# Revit family: Door-Exterior-Simpson-Nantucket-Full_Glass-Single
name_source: partatom
category: Doors
revit_build: Autodesk Revit Architecture 2012 (Build: 20110916_2132(x64)
units: mm (PartAtom-declared; Revit-internal decimal feet)

## types (219) — shared parameters
Assembly Code = B2030230
Construction Type = Wood
Frame = Wood - Simpson Doors - Douglas Fir
Frame Projection Ext. = 0' - 1"
Frame Projection Int. = 0' - 1"
Frame Type = Frame : Standard
Frame Width = 0' - 3"
Function = Exterior
Glass = Glass - Simpson Doors - Clear
Manufacturer = Simpsons Door Company
Ovolo Construction = Yes
Panel = Wood - Simpson Doors - Douglas Fir
Panel Stile Width = 0' - 5"
Product Documentation Link = http://www.simpsondoor.com
Product Page URL = http://www.simpsondoor.com
Thickness = 0' - 1 3/4"
Thickness Note = comes in 1 3/4" and 2 1/4" Thickness. Default is set to 1 3/4"
URL = http://www.simpsondoor.com
Wall Closure = By host

## per-type parameters (varying)
| type | Bottom Rail Height | Description | Height | Horizontal Outside Muntin | Middle Rail | Model | Number of Horizontal Muntins | Number of Vertical Muntins | Rough Height | Rough Width | Top Rail Height | Vertical Outside Muntin | Width |
| 77002 Nantucket 30x80 Ovolo Flat Panel | 0' - 8 11/16" | Nantucket - Single Lite | 6' - 8" | No | No | 77002 | 0 | 0 | 6' - 10" | 2' - 10" | 0' - 4 15/16" | No | 2' - 6" |
| 77002 Nantucket 30x84 Ovolo Flat Panel | 0' - 8 11/16" | Nantucket - Single Lite | 7' - 0" | No | No | 77002 | 0 | 0 | 7' - 2" | 2' - 10" | 0' - 4 15/16" | No | 2' - 6" |
| 77002 Nantucket 30x96 Ovolo Flat Panel | 0' - 8 11/16" | Nantucket - Single Lite | 8' - 0" | No | No | 77002 | 0 | 0 | 8' - 2" | 2' - 10" | 0' - 4 15/16" | No | 2' - 6" |
| 77002 Nantucket 32x80 Ovolo Flat Panel | 0' - 8 11/16" | Nantucket - Single Lite | 6' - 8" | No | No | 77002 | 0 | 0 | 6' - 10" | 3' - 0" | 0' - 4 15/16" | No | 2' - 8" |
| 77002 Nantucket 32x84 Ovolo Flat Panel | 0' - 8 11/16" | Nantucket - Single Lite | 7' - 0" | No | No | 77002 | 0 | 0 | 7' - 2" | 3' - 0" | 0' - 4 15/16" | No | 2' - 8" |
| 77002 Nantucket 32x96 Ovolo Flat Panel | 0' - 8 11/16" | Nantucket - Single Lite | 8' - 0" | No | No | 77002 | 0 | 0 | 8' - 2" | 3' - 0" | 0' - 4 15/16" | No | 2' - 8" |
| 77002 Nantucket 34x80 Ovolo Flat Panel | 0' - 8 11/16" | Nantucket - Single Lite | 6' - 8" | No | No | 77002 | 0 | 0 | 6' - 10" | 3' - 2" | 0' - 4 15/16" | No | 2' - 10" |
| 77002 Nantucket 34x84 Ovolo Flat Panel | 0' - 8 11/16" | Nantucket - Single Lite | 7' - 0" | No | No | 77002 | 0 | 0 | 7' - 2" | 3' - 2" | 0' - 4 15/16" | No | 2' - 10" |
| 77002 Nantucket 34x96 Ovolo Flat Panel | 0' - 8 11/16" | Nantucket - Single Lite | 8' - 0" | No | No | 77002 | 0 | 0 | 8' - 2" | 3' - 2" | 0' - 4 15/16" | No | 2' - 10" |
| 77002 Nantucket 36x80 Ovolo Flat Panel | 0' - 8 11/16" | Nantucket - Single Lite | 6' - 8" | No | No | 77002 | 0 | 0 | 6' - 10" | 3' - 4" | 0' - 4 15/16" | No | 3' - 0" |
| 77002 Nantucket 36x84 Ovolo Flat Panel | 0' - 8 11/16" | Nantucket - Single Lite | 7' - 0" | No | No | 77002 | 0 | 0 | 7' - 2" | 3' - 4" | 0' - 4 15/16" | No | 3' - 0" |
| 77002 Nantucket 36x96 Ovolo Flat Panel | 0' - 8 11/16" | Nantucket - Single Lite | 8' - 0" | No | No | 77002 | 0 | 0 | 8' - 2" | 3' - 4" | 0' - 4 15/16" | No | 3' - 0" |
| 77002 Nantucket 38x80 Ovolo Flat Panel | 0' - 8 11/16" | Nantucket - Single Lite | 6' - 8" | No | No | 77002 | 0 | 0 | 6' - 10" | 3' - 6" | 0' - 4 15/16" | No | 3' - 2" |
| 77002 Nantucket 38x84 Ovolo Flat Panel | 0' - 8 11/16" | Nantucket - Single Lite | 7' - 0" | No | No | 77002 | 0 | 0 | 7' - 2" | 3' - 6" | 0' - 4 15/16" | No | 3' - 2" |
| 77002 Nantucket 38x96 Ovolo Flat Panel | 0' - 8 11/16" | Nantucket - Single Lite | 8' - 0" | No | No | 77002 | 0 | 0 | 8' - 2" | 3' - 6" | 0' - 4 15/16" | No | 3' - 2" |
| 77002 Nantucket 40x80 Ovolo Flat Panel | 0' - 8 11/16" | Nantucket - Single Lite | 6' - 8" | No | No | 77002 | 0 | 0 | 6' - 10" | 3' - 8" | 0' - 4 15/16" | No | 3' - 4" |
| 77002 Nantucket 40x84 Ovolo Flat Panel | 0' - 8 11/16" | Nantucket - Single Lite | 7' - 0" | No | No | 77002 | 0 | 0 | 7' - 2" | 3' - 8" | 0' - 4 15/16" | No | 3' - 4" |
| 77002 Nantucket 40x96 Ovolo Flat Panel | 0' - 8 11/16" | Nantucket - Single Lite | 8' - 0" | No | No | 77002 | 0 | 0 | 8' - 2" | 3' - 8" | 0' - 4 15/16" | No | 3' - 4" |
| 77010 Nantucket 30x80 Ovolo Flat Panel | 0' - 8 11/16" | Nantucket - Ten Lite | 6' - 8" | No | No | 77010 | 4 | 1 | 6' - 10" | 2' - 10" | 0' - 4 15/16" | No | 2' - 6" |
| 77010 Nantucket 30x84 Ovolo Flat Panel | 0' - 8 11/16" | Nantucket - Ten Lite | 7' - 0" | No | No | 77010 | 4 | 1 | 7' - 2" | 2' - 10" | 0' - 4 15/16" | No | 2' - 6" |
| 77010 Nantucket 30x96 Ovolo Flat Panel | 0' - 8 11/16" | Nantucket - Ten Lite | 8' - 0" | No | No | 77010 | 4 | 1 | 8' - 2" | 2' - 10" | 0' - 4 15/16" | No | 2' - 6" |
| 77010 Nantucket 32x80 Ovolo Flat Panel | 0' - 8 11/16" | Nantucket - Ten Lite | 6' - 8" | No | No | 77010 | 4 | 1 | 6' - 10" | 3' - 0" | 0' - 4 15/16" | No | 2' - 8" |
| 77010 Nantucket 32x84 Ovolo Flat Panel | 0' - 8 11/16" | Nantucket - Ten Lite | 7' - 0" | No | No | 77010 | 4 | 1 | 7' - 2" | 3' - 0" | 0' - 4 15/16" | No | 2' - 8" |
| 77010 Nantucket 32x96 Ovolo Flat Panel | 0' - 8 11/16" | Nantucket - Ten Lite | 8' - 0" | No | No | 77010 | 4 | 1 | 8' - 2" | 3' - 0" | 0' - 4 15/16" | No | 2' - 8" |
| 77010 Nantucket 34x80 Ovolo Flat Panel | 0' - 8 11/16" | Nantucket - Ten Lite | 6' - 8" | No | No | 77010 | 4 | 1 | 6' - 10" | 3' - 2" | 0' - 4 15/16" | No | 2' - 10" |
| 77010 Nantucket 34x84 Ovolo Flat Panel | 0' - 8 11/16" | Nantucket - Ten Lite | 7' - 0" | No | No | 77010 | 4 | 1 | 7' - 2" | 3' - 2" | 0' - 4 15/16" | No | 2' - 10" |
| 77010 Nantucket 34x96 Ovolo Flat Panel | 0' - 8 11/16" | Nantucket - Ten Lite | 8' - 0" | No | No | 77010 | 4 | 1 | 8' - 2" | 3' - 2" | 0' - 4 15/16" | No | 2' - 10" |
| 77010 Nantucket 36x80 Ovolo Flat Panel | 0' - 8 11/16" | Nantucket - Ten Lite | 6' - 8" | No | No | 77010 | 4 | 1 | 6' - 10" | 3' - 4" | 0' - 4 15/16" | No | 3' - 0" |
| 77010 Nantucket 36x84 Ovolo Flat Panel | 0' - 8 11/16" | Nantucket - Ten Lite | 7' - 0" | No | No | 77010 | 4 | 1 | 7' - 2" | 3' - 4" | 0' - 4 15/16" | No | 3' - 0" |
| 77010 Nantucket 36x96 Ovolo Flat Panel | 0' - 8 11/16" | Nantucket - Ten Lite | 8' - 0" | No | No | 77010 | 4 | 1 | 8' - 2" | 3' - 4" | 0' - 4 15/16" | No | 3' - 0" |
| 77010 Nantucket 38x80 Ovolo Flat Panel | 0' - 8 11/16" | Nantucket - Ten Lite | 6' - 8" | No | No | 77010 | 4 | 1 | 6' - 10" | 3' - 6" | 0' - 4 15/16" | No | 3' - 2" |
| 77010 Nantucket 38x84 Ovolo Flat Panel | 0' - 8 11/16" | Nantucket - Ten Lite | 7' - 0" | No | No | 77010 | 4 | 1 | 7' - 2" | 3' - 6" | 0' - 4 15/16" | No | 3' - 2" |
| 77010 Nantucket 38x96 Ovolo Flat Panel | 0' - 8 11/16" | Nantucket - Ten Lite | 8' - 0" | No | No | 77010 | 4 | 1 | 8' - 2" | 3' - 6" | 0' - 4 15/16" | No | 3' - 2" |
| 77010 Nantucket 40x80 Ovolo Flat Panel | 0' - 8 11/16" | Nantucket - Ten Lite | 6' - 8" | No | No | 77010 | 4 | 1 | 6' - 10" | 3' - 8" | 0' - 4 15/16" | No | 3' - 4" |
| 77010 Nantucket 40x84 Ovolo Flat Panel | 0' - 8 11/16" | Nantucket - Ten Lite | 7' - 0" | No | No | 77010 | 4 | 1 | 7' - 2" | 3' - 8" | 0' - 4 15/16" | No | 3' - 4" |
| 77010 Nantucket 40x96 Ovolo Flat Panel | 0' - 8 11/16" | Nantucket - Ten Lite | 8' - 0" | No | No | 77010 | 4 | 1 | 8' - 2" | 3' - 8" | 0' - 4 15/16" | No | 3' - 4" |
| 77015 Nantucket 30x80 Ovolo Flat Panel | 0' - 8 11/16" | Nantucket - Fifteen Lite | 6' - 8" | No | No | 77015 | 4 | 2 | 6' - 10" | 2' - 10" | 0' - 4 15/16" | No | 2' - 6" |
| 77015 Nantucket 30x84 Ovolo Flat Panel | 0' - 8 11/16" | Nantucket - Fifteen Lite | 7' - 0" | No | No | 77015 | 4 | 2 | 7' - 2" | 2' - 10" | 0' - 4 15/16" | No | 2' - 6" |
| 77015 Nantucket 30x96 Ovolo Flat Panel | 0' - 8 11/16" | Nantucket - Fifteen Lite | 8' - 0" | No | No | 77015 | 4 | 2 | 8' - 2" | 2' - 10" | 0' - 4 15/16" | No | 2' - 6" |
| 77015 Nantucket 32x80 Ovolo Flat Panel | 0' - 8 11/16" | Nantucket - Fifteen Lite | 6' - 8" | No | No | 77015 | 4 | 2 | 6' - 10" | 3' - 0" | 0' - 4 15/16" | No | 2' - 8" |
| 77015 Nantucket 32x84 Ovolo Flat Panel | 0' - 8 11/16" | Nantucket - Fifteen Lite | 7' - 0" | No | No | 77015 | 4 | 2 | 7' - 2" | 3' - 0" | 0' - 4 15/16" | No | 2' - 8" |
| 77015 Nantucket 32x96 Ovolo Flat Panel | 0' - 8 11/16" | Nantucket - Fifteen Lite | 8' - 0" | No | No | 77015 | 4 | 2 | 8' - 2" | 3' - 0" | 0' - 4 15/16" | No | 2' - 8" |
| 77015 Nantucket 34x80 Ovolo Flat Panel | 0' - 8 11/16" | Nantucket - Fifteen Lite | 6' - 8" | No | No | 77015 | 4 | 2 | 6' - 10" | 3' - 2" | 0' - 4 15/16" | No | 2' - 10" |
| 77015 Nantucket 34x84 Ovolo Flat Panel | 0' - 8 11/16" | Nantucket - Fifteen Lite | 7' - 0" | No | No | 77015 | 4 | 2 | 7' - 2" | 3' - 2" | 0' - 4 15/16" | No | 2' - 10" |
| 77015 Nantucket 34x96 Ovolo Flat Panel | 0' - 8 11/16" | Nantucket - Fifteen Lite | 8' - 0" | No | No | 77015 | 4 | 2 | 8' - 2" | 3' - 2" | 0' - 4 15/16" | No | 2' - 10" |
| 77015 Nantucket 36x80 Ovolo Flat Panel | 0' - 8 11/16" | Nantucket - Fifteen Lite | 6' - 8" | No | No | 77015 | 4 | 2 | 6' - 10" | 3' - 4" | 0' - 4 15/16" | No | 3' - 0" |
| 77015 Nantucket 36x84 Ovolo Flat Panel | 0' - 8 11/16" | Nantucket - Fifteen Lite | 7' - 0" | No | No | 77015 | 4 | 2 | 7' - 2" | 3' - 4" | 0' - 4 15/16" | No | 3' - 0" |
| 77015 Nantucket 36x96 Ovolo Flat Panel | 0' - 8 11/16" | Nantucket - Fifteen Lite | 8' - 0" | No | No | 77015 | 4 | 2 | 8' - 2" | 3' - 4" | 0' - 4 15/16" | No | 3' - 0" |
| 77015 Nantucket 38x80 Ovolo Flat Panel | 0' - 8 11/16" | Nantucket - Fifteen Lite | 6' - 8" | No | No | 77015 | 4 | 2 | 6' - 10" | 3' - 6" | 0' - 4 15/16" | No | 3' - 2" |
| 77015 Nantucket 38x84 Ovolo Flat Panel | 0' - 8 11/16" | Nantucket - Fifteen Lite | 7' - 0" | No | No | 77015 | 4 | 2 | 7' - 2" | 3' - 6" | 0' - 4 15/16" | No | 3' - 2" |
| 77015 Nantucket 38x96 Ovolo Flat Panel | 0' - 8 11/16" | Nantucket - Fifteen Lite | 8' - 0" | No | No | 77015 | 4 | 2 | 8' - 2" | 3' - 6" | 0' - 4 15/16" | No | 3' - 2" |
| 77015 Nantucket 40x80 Ovolo Flat Panel | 0' - 8 11/16" | Nantucket - Fifteen Lite | 6' - 8" | No | No | 77015 | 4 | 2 | 6' - 10" | 3' - 8" | 0' - 4 15/16" | No | 3' - 4" |
| 77015 Nantucket 40x84 Ovolo Flat Panel | 0' - 8 11/16" | Nantucket - Fifteen Lite | 7' - 0" | No | No | 77015 | 4 | 2 | 7' - 2" | 3' - 8" | 0' - 4 15/16" | No | 3' - 4" |
| 77015 Nantucket 40x96 Ovolo Flat Panel | 0' - 8 11/16" | Nantucket - Fifteen Lite | 8' - 0" | No | No | 77015 | 4 | 2 | 8' - 2" | 3' - 8" | 0' - 4 15/16" | No | 3' - 4" |
| 77037 Nantucket 30x80 Ovolo Flat Panel | 1' - 6" | Nantucket - Single Lite | 6' - 8" | No | No | 77037 | 0 | 0 | 6' - 10" | 2' - 10" | 0' - 5 15/16" | No | 2' - 6" |
| 77037 Nantucket 30x84 Ovolo Flat Panel | 1' - 6" | Nantucket - Single Lite | 7' - 0" | No | No | 77037 | 0 | 0 | 7' - 2" | 2' - 10" | 0' - 5 15/16" | No | 2' - 6" |
| 77037 Nantucket 30x96 Ovolo Flat Panel | 1' - 6" | Nantucket - Single Lite | 8' - 0" | No | No | 77037 | 0 | 0 | 8' - 2" | 2' - 10" | 0' - 5 15/16" | No | 2' - 6" |
| 77037 Nantucket 32x80 Ovolo Flat Panel | 1' - 6" | Nantucket - Single Lite | 6' - 8" | No | No | 77037 | 0 | 0 | 6' - 10" | 3' - 0" | 0' - 5 15/16" | No | 2' - 8" |
| 77037 Nantucket 32x84 Ovolo Flat Panel | 1' - 6" | Nantucket - Single Lite | 7' - 0" | No | No | 77037 | 0 | 0 | 7' - 2" | 3' - 0" | 0' - 5 15/16" | No | 2' - 8" |
| 77037 Nantucket 32x96 Ovolo Flat Panel | 1' - 6" | Nantucket - Single Lite | 8' - 0" | No | No | 77037 | 0 | 0 | 8' - 2" | 3' - 0" | 0' - 5 15/16" | No | 2' - 8" |
| 77037 Nantucket 34x80 Ovolo Flat Panel | 1' - 6" | Nantucket - Single Lite | 6' - 8" | No | No | 77037 | 0 | 0 | 6' - 10" | 3' - 2" | 0' - 5 15/16" | No | 2' - 10" |
| 77037 Nantucket 34x84 Ovolo Flat Panel | 1' - 6" | Nantucket - Single Lite | 7' - 0" | No | No | 77037 | 0 | 0 | 7' - 2" | 3' - 2" | 0' - 5 15/16" | No | 2' - 10" |
| 77037 Nantucket 34x96 Ovolo Flat Panel | 1' - 6" | Nantucket - Single Lite | 8' - 0" | No | No | 77037 | 0 | 0 | 8' - 2" | 3' - 2" | 0' - 5 15/16" | No | 2' - 10" |
| 77037 Nantucket 36x80 Ovolo Flat Panel | 1' - 6" | Nantucket - Single Lite | 6' - 8" | No | No | 77037 | 0 | 0 | 6' - 10" | 3' - 4" | 0' - 5 15/16" | No | 3' - 0" |
| 77037 Nantucket 36x84 Ovolo Flat Panel | 1' - 6" | Nantucket - Single Lite | 7' - 0" | No | No | 77037 | 0 | 0 | 7' - 2" | 3' - 4" | 0' - 5 15/16" | No | 3' - 0" |
| 77037 Nantucket 36x96 Ovolo Flat Panel | 1' - 6" | Nantucket - Single Lite | 8' - 0" | No | No | 77037 | 0 | 0 | 8' - 2" | 3' - 4" | 0' - 5 15/16" | No | 3' - 0" |
| 77037 Nantucket 38x80 Ovolo Flat Panel | 1' - 6" | Nantucket - Single Lite | 6' - 8" | No | No | 77037 | 0 | 0 | 6' - 10" | 3' - 6" | 0' - 5 15/16" | No | 3' - 2" |
| 77037 Nantucket 38x84 Ovolo Flat Panel | 1' - 6" | Nantucket - Single Lite | 7' - 0" | No | No | 77037 | 0 | 0 | 7' - 2" | 3' - 6" | 0' - 5 15/16" | No | 3' - 2" |
| 77037 Nantucket 38x96 Ovolo Flat Panel | 1' - 6" | Nantucket - Single Lite | 8' - 0" | No | No | 77037 | 0 | 0 | 8' - 2" | 3' - 6" | 0' - 5 15/16" | No | 3' - 2" |
| 77037 Nantucket 40x80 Ovolo Flat Panel | 1' - 6" | Nantucket - Single Lite | 6' - 8" | No | No | 77037 | 0 | 0 | 6' - 10" | 3' - 8" | 0' - 5 15/16" | No | 3' - 4" |
| 77037 Nantucket 40x84 Ovolo Flat Panel | 1' - 6" | Nantucket - Single Lite | 7' - 0" | No | No | 77037 | 0 | 0 | 7' - 2" | 3' - 8" | 0' - 5 15/16" | No | 3' - 4" |
| 77037 Nantucket 40x96 Ovolo Flat Panel | 1' - 6" | Nantucket - Single Lite | 8' - 0" | No | No | 77037 | 0 | 0 | 8' - 2" | 3' - 8" | 0' - 5 15/16" | No | 3' - 4" |
| 77082 Nantucket 30x80 Ovolo Flat Panel | 0' - 8 11/16" | Nantucket - Two Lite | 6' - 8" | No | Yes | 77082 | 0 | 0 | 6' - 10" | 2' - 10" | 0' - 4 15/16" | No | 2' - 6" |
| 77082 Nantucket 30x84 Ovolo Flat Panel | 0' - 8 11/16" | Nantucket - Two Lite | 7' - 0" | No | Yes | 77082 | 0 | 0 | 7' - 2" | 2' - 10" | 0' - 4 15/16" | No | 2' - 6" |
| 77082 Nantucket 30x96 Ovolo Flat Panel | 0' - 8 11/16" | Nantucket - Two Lite | 8' - 0" | No | Yes | 77082 | 0 | 0 | 8' - 2" | 2' - 10" | 0' - 4 15/16" | No | 2' - 6" |
| 77082 Nantucket 32x80 Ovolo Flat Panel | 0' - 8 11/16" | Nantucket - Two Lite | 6' - 8" | No | Yes | 77082 | 0 | 0 | 6' - 10" | 3' - 0" | 0' - 4 15/16" | No | 2' - 8" |
| 77082 Nantucket 32x84 Ovolo Flat Panel | 0' - 8 11/16" | Nantucket - Two Lite | 7' - 0" | No | Yes | 77082 | 0 | 0 | 7' - 2" | 3' - 0" | 0' - 4 15/16" | No | 2' - 8" |
| 77082 Nantucket 32x96 Ovolo Flat Panel | 0' - 8 11/16" | Nantucket - Two Lite | 8' - 0" | No | Yes | 77082 | 0 | 0 | 8' - 2" | 3' - 0" | 0' - 4 15/16" | No | 2' - 8" |
| 77082 Nantucket 34x80 Ovolo Flat Panel | 0' - 8 11/16" | Nantucket - Two Lite | 6' - 8" | No | Yes | 77082 | 0 | 0 | 6' - 10" | 3' - 2" | 0' - 4 15/16" | No | 2' - 10" |
| 77082 Nantucket 34x84 Ovolo Flat Panel | 0' - 8 11/16" | Nantucket - Two Lite | 7' - 0" | No | Yes | 77082 | 0 | 0 | 7' - 2" | 3' - 2" | 0' - 4 15/16" | No | 2' - 10" |
| 77082 Nantucket 34x96 Ovolo Flat Panel | 0' - 8 11/16" | Nantucket - Two Lite | 8' - 0" | No | Yes | 77082 | 0 | 0 | 8' - 2" | 3' - 2" | 0' - 4 15/16" | No | 2' - 10" |
| 77082 Nantucket 36x80 Ovolo Flat Panel | 0' - 8 11/16" | Nantucket - Two Lite | 6' - 8" | No | Yes | 77082 | 0 | 0 | 6' - 10" | 3' - 4" | 0' - 4 15/16" | No | 3' - 0" |
| 77082 Nantucket 36x84 Ovolo Flat Panel | 0' - 8 11/16" | Nantucket - Two Lite | 7' - 0" | No | Yes | 77082 | 0 | 0 | 7' - 2" | 3' - 4" | 0' - 4 15/16" | No | 3' - 0" |
| 77082 Nantucket 36x96 Ovolo Flat Panel | 0' - 8 11/16" | Nantucket - Two Lite | 8' - 0" | No | Yes | 77082 | 0 | 0 | 8' - 2" | 3' - 4" | 0' - 4 15/16" | No | 3' - 0" |
| 77082 Nantucket 38x80 Ovolo Flat Panel | 0' - 8 11/16" | Nantucket - Two Lite | 6' - 8" | No | Yes | 77082 | 0 | 0 | 6' - 10" | 3' - 6" | 0' - 4 15/16" | No | 3' - 2" |
| 77082 Nantucket 38x84 Ovolo Flat Panel | 0' - 8 11/16" | Nantucket - Two Lite | 7' - 0" | No | Yes | 77082 | 0 | 0 | 7' - 2" | 3' - 6" | 0' - 4 15/16" | No | 3' - 2" |
| 77082 Nantucket 38x96 Ovolo Flat Panel | 0' - 8 11/16" | Nantucket - Two Lite | 8' - 0" | No | Yes | 77082 | 0 | 0 | 8' - 2" | 3' - 6" | 0' - 4 15/16" | No | 3' - 2" |
| 77082 Nantucket 40x80 Ovolo Flat Panel | 0' - 8 11/16" | Nantucket - Two Lite | 6' - 8" | No | Yes | 77082 | 0 | 0 | 6' - 10" | 3' - 8" | 0' - 4 15/16" | No | 3' - 4" |
| 77082 Nantucket 40x84 Ovolo Flat Panel | 0' - 8 11/16" | Nantucket - Two Lite | 7' - 0" | No | Yes | 77082 | 0 | 0 | 7' - 2" | 3' - 8" | 0' - 4 15/16" | No | 3' - 4" |
| 77082 Nantucket 40x96 Ovolo Flat Panel | 0' - 8 11/16" | Nantucket - Two Lite | 8' - 0" | No | Yes | 77082 | 0 | 0 | 8' - 2" | 3' - 8" | 0' - 4 15/16" | No | 3' - 4" |
| 77082 Nantucket 42x80 Ovolo Flat Panel | 0' - 8 11/16" | Nantucket - Two Lite | 6' - 8" | No | Yes | 77082 | 0 | 0 | 6' - 10" | 3' - 10" | 0' - 4 15/16" | No | 3' - 6" |
| 77082 Nantucket 42x84 Ovolo Flat Panel | 0' - 8 11/16" | Nantucket - Two Lite | 7' - 0" | No | Yes | 77082 | 0 | 0 | 7' - 2" | 3' - 10" | 0' - 4 15/16" | No | 3' - 6" |
| 77082 Nantucket 42x96 Ovolo Flat Panel | 0' - 8 11/16" | Nantucket - Two Lite | 8' - 0" | No | Yes | 77082 | 0 | 0 | 8' - 2" | 3' - 10" | 0' - 4 15/16" | No | 3' - 6" |
| 77103 Nantucket 30x80 Ovolo Flat Panel | 0' - 8 11/16" | Nantucket - Three Lite | 6' - 8" | No | No | 77103 | 2 | 0 | 6' - 10" | 2' - 10" | 0' - 4 15/16" | No | 2' - 6" |
| 77103 Nantucket 30x84 Ovolo Flat Panel | 0' - 8 11/16" | Nantucket - Three Lite | 7' - 0" | No | No | 77103 | 2 | 0 | 7' - 2" | 2' - 10" | 0' - 4 15/16" | No | 2' - 6" |
| 77103 Nantucket 30x96 Ovolo Flat Panel | 0' - 8 11/16" | Nantucket - Three Lite | 8' - 0" | No | No | 77103 | 2 | 0 | 8' - 2" | 2' - 10" | 0' - 4 15/16" | No | 2' - 6" |
| 77103 Nantucket 32x80 Ovolo Flat Panel | 0' - 8 11/16" | Nantucket - Three Lite | 6' - 8" | No | No | 77103 | 2 | 0 | 6' - 10" | 3' - 0" | 0' - 4 15/16" | No | 2' - 8" |
| 77103 Nantucket 32x84 Ovolo Flat Panel | 0' - 8 11/16" | Nantucket - Three Lite | 7' - 0" | No | No | 77103 | 2 | 0 | 7' - 2" | 3' - 0" | 0' - 4 15/16" | No | 2' - 8" |
| 77103 Nantucket 32x96 Ovolo Flat Panel | 0' - 8 11/16" | Nantucket - Three Lite | 8' - 0" | No | No | 77103 | 2 | 0 | 8' - 2" | 3' - 0" | 0' - 4 15/16" | No | 2' - 8" |
| 77103 Nantucket 34x80 Ovolo Flat Panel | 0' - 8 11/16" | Nantucket - Three Lite | 6' - 8" | No | No | 77103 | 2 | 0 | 6' - 10" | 3' - 2" | 0' - 4 15/16" | No | 2' - 10" |
| 77103 Nantucket 34x84 Ovolo Flat Panel | 0' - 8 11/16" | Nantucket - Three Lite | 7' - 0" | No | No | 77103 | 2 | 0 | 7' - 2" | 3' - 2" | 0' - 4 15/16" | No | 2' - 10" |
| 77103 Nantucket 34x96 Ovolo Flat Panel | 0' - 8 11/16" | Nantucket - Three Lite | 8' - 0" | No | No | 77103 | 2 | 0 | 8' - 2" | 3' - 2" | 0' - 4 15/16" | No | 2' - 10" |
| 77103 Nantucket 36x80 Ovolo Flat Panel | 0' - 8 11/16" | Nantucket - Three Lite | 6' - 8" | No | No | 77103 | 2 | 0 | 6' - 10" | 3' - 4" | 0' - 4 15/16" | No | 3' - 0" |
| 77103 Nantucket 36x84 Ovolo Flat Panel | 0' - 8 11/16" | Nantucket - Three Lite | 7' - 0" | No | No | 77103 | 2 | 0 | 7' - 2" | 3' - 4" | 0' - 4 15/16" | No | 3' - 0" |
| 77103 Nantucket 36x96 Ovolo Flat Panel | 0' - 8 11/16" | Nantucket - Three Lite | 8' - 0" | No | No | 77103 | 2 | 0 | 8' - 2" | 3' - 4" | 0' - 4 15/16" | No | 3' - 0" |
| 77103 Nantucket 38x80 Ovolo Flat Panel | 0' - 8 11/16" | Nantucket - Three Lite | 6' - 8" | No | No | 77103 | 2 | 0 | 6' - 10" | 3' - 6" | 0' - 4 15/16" | No | 3' - 2" |
| 77103 Nantucket 38x84 Ovolo Flat Panel | 0' - 8 11/16" | Nantucket - Three Lite | 7' - 0" | No | No | 77103 | 2 | 0 | 7' - 2" | 3' - 6" | 0' - 4 15/16" | No | 3' - 2" |
| 77103 Nantucket 38x96 Ovolo Flat Panel | 0' - 8 11/16" | Nantucket - Three Lite | 8' - 0" | No | No | 77103 | 2 | 0 | 8' - 2" | 3' - 6" | 0' - 4 15/16" | No | 3' - 2" |
| 77103 Nantucket 40x80 Ovolo Flat Panel | 0' - 8 11/16" | Nantucket - Three Lite | 6' - 8" | No | No | 77103 | 2 | 0 | 6' - 10" | 3' - 8" | 0' - 4 15/16" | No | 3' - 4" |
| 77103 Nantucket 40x84 Ovolo Flat Panel | 0' - 8 11/16" | Nantucket - Three Lite | 7' - 0" | No | No | 77103 | 2 | 0 | 7' - 2" | 3' - 8" | 0' - 4 15/16" | No | 3' - 4" |
| 77103 Nantucket 40x96 Ovolo Flat Panel | 0' - 8 11/16" | Nantucket - Three Lite | 8' - 0" | No | No | 77103 | 2 | 0 | 8' - 2" | 3' - 8" | 0' - 4 15/16" | No | 3' - 4" |
| 77104 Nantucket 30x80 Ovolo Flat Panel | 0' - 8 11/16" | Nantucket - Four Lite | 6' - 8" | No | No | 77104 | 3 | 0 | 6' - 10" | 2' - 10" | 0' - 4 15/16" | No | 2' - 6" |
| 77104 Nantucket 30x84 Ovolo Flat Panel | 0' - 8 11/16" | Nantucket - Four Lite | 7' - 0" | No | No | 77104 | 3 | 0 | 7' - 2" | 2' - 10" | 0' - 4 15/16" | No | 2' - 6" |
| 77104 Nantucket 30x96 Ovolo Flat Panel | 0' - 8 11/16" | Nantucket - Four Lite | 8' - 0" | No | No | 77104 | 3 | 0 | 8' - 2" | 2' - 10" | 0' - 4 15/16" | No | 2' - 6" |
| 77104 Nantucket 32x80 Ovolo Flat Panel | 0' - 8 11/16" | Nantucket - Four Lite | 6' - 8" | No | No | 77104 | 3 | 0 | 6' - 10" | 3' - 0" | 0' - 4 15/16" | No | 2' - 8" |
| 77104 Nantucket 32x84 Ovolo Flat Panel | 0' - 8 11/16" | Nantucket - Four Lite | 7' - 0" | No | No | 77104 | 3 | 0 | 7' - 2" | 3' - 0" | 0' - 4 15/16" | No | 2' - 8" |
| 77104 Nantucket 32x96 Ovolo Flat Panel | 0' - 8 11/16" | Nantucket - Four Lite | 8' - 0" | No | No | 77104 | 3 | 0 | 8' - 2" | 3' - 0" | 0' - 4 15/16" | No | 2' - 8" |
| 77104 Nantucket 34x80 Ovolo Flat Panel | 0' - 8 11/16" | Nantucket - Four Lite | 6' - 8" | No | No | 77104 | 3 | 0 | 6' - 10" | 3' - 2" | 0' - 4 15/16" | No | 2' - 10" |
| 77104 Nantucket 34x84 Ovolo Flat Panel | 0' - 8 11/16" | Nantucket - Four Lite | 7' - 0" | No | No | 77104 | 3 | 0 | 7' - 2" | 3' - 2" | 0' - 4 15/16" | No | 2' - 10" |
| 77104 Nantucket 34x96 Ovolo Flat Panel | 0' - 8 11/16" | Nantucket - Four Lite | 8' - 0" | No | No | 77104 | 3 | 0 | 8' - 2" | 3' - 2" | 0' - 4 15/16" | No | 2' - 10" |
| 77104 Nantucket 36x80 Ovolo Flat Panel | 0' - 8 11/16" | Nantucket - Four Lite | 6' - 8" | No | No | 77104 | 3 | 0 | 6' - 10" | 3' - 4" | 0' - 4 15/16" | No | 3' - 0" |
| 77104 Nantucket 36x84 Ovolo Flat Panel | 0' - 8 11/16" | Nantucket - Four Lite | 7' - 0" | No | No | 77104 | 3 | 0 | 7' - 2" | 3' - 4" | 0' - 4 15/16" | No | 3' - 0" |
| 77104 Nantucket 36x96 Ovolo Flat Panel | 0' - 8 11/16" | Nantucket - Four Lite | 8' - 0" | No | No | 77104 | 3 | 0 | 8' - 2" | 3' - 4" | 0' - 4 15/16" | No | 3' - 0" |
| 77104 Nantucket 38x80 Ovolo Flat Panel | 0' - 8 11/16" | Nantucket - Four Lite | 6' - 8" | No | No | 77104 | 3 | 0 | 6' - 10" | 3' - 6" | 0' - 4 15/16" | No | 3' - 2" |
| 77104 Nantucket 38x84 Ovolo Flat Panel | 0' - 8 11/16" | Nantucket - Four Lite | 7' - 0" | No | No | 77104 | 3 | 0 | 7' - 2" | 3' - 6" | 0' - 4 15/16" | No | 3' - 2" |
| 77104 Nantucket 38x96 Ovolo Flat Panel | 0' - 8 11/16" | Nantucket - Four Lite | 8' - 0" | No | No | 77104 | 3 | 0 | 8' - 2" | 3' - 6" | 0' - 4 15/16" | No | 3' - 2" |
| 77104 Nantucket 40x80 Ovolo Flat Panel | 0' - 8 11/16" | Nantucket - Four Lite | 6' - 8" | No | No | 77104 | 3 | 0 | 6' - 10" | 3' - 8" | 0' - 4 15/16" | No | 3' - 4" |
| 77104 Nantucket 40x84 Ovolo Flat Panel | 0' - 8 11/16" | Nantucket - Four Lite | 7' - 0" | No | No | 77104 | 3 | 0 | 7' - 2" | 3' - 8" | 0' - 4 15/16" | No | 3' - 4" |
| 77104 Nantucket 40x96 Ovolo Flat Panel | 0' - 8 11/16" | Nantucket - Four Lite | 8' - 0" | No | No | 77104 | 3 | 0 | 8' - 2" | 3' - 8" | 0' - 4 15/16" | No | 3' - 4" |
| 77105 Nantucket 30x80 Ovolo Flat Panel | 0' - 8 11/16" | Nantucket - Five Lite | 6' - 8" | No | No | 77105 | 4 | 0 | 6' - 10" | 2' - 10" | 0' - 4 15/16" | No | 2' - 6" |
| 77105 Nantucket 30x84 Ovolo Flat Panel | 0' - 8 11/16" | Nantucket - Five Lite | 7' - 0" | No | No | 77105 | 4 | 0 | 7' - 2" | 2' - 10" | 0' - 4 15/16" | No | 2' - 6" |
| 77105 Nantucket 30x96 Ovolo Flat Panel | 0' - 8 11/16" | Nantucket - Five Lite | 8' - 0" | No | No | 77105 | 4 | 0 | 8' - 2" | 2' - 10" | 0' - 4 15/16" | No | 2' - 6" |
| 77105 Nantucket 32x80 Ovolo Flat Panel | 0' - 8 11/16" | Nantucket - Five Lite | 6' - 8" | No | No | 77105 | 4 | 0 | 6' - 10" | 3' - 0" | 0' - 4 15/16" | No | 2' - 8" |
| 77105 Nantucket 32x84 Ovolo Flat Panel | 0' - 8 11/16" | Nantucket - Five Lite | 7' - 0" | No | No | 77105 | 4 | 0 | 7' - 2" | 3' - 0" | 0' - 4 15/16" | No | 2' - 8" |
| 77105 Nantucket 32x96 Ovolo Flat Panel | 0' - 8 11/16" | Nantucket - Five Lite | 8' - 0" | No | No | 77105 | 4 | 0 | 8' - 2" | 3' - 0" | 0' - 4 15/16" | No | 2' - 8" |
| 77105 Nantucket 34x80 Ovolo Flat Panel | 0' - 8 11/16" | Nantucket - Five Lite | 6' - 8" | No | No | 77105 | 4 | 0 | 6' - 10" | 3' - 2" | 0' - 4 15/16" | No | 2' - 10" |
| 77105 Nantucket 34x84 Ovolo Flat Panel | 0' - 8 11/16" | Nantucket - Five Lite | 7' - 0" | No | No | 77105 | 4 | 0 | 7' - 2" | 3' - 2" | 0' - 4 15/16" | No | 2' - 10" |
| 77105 Nantucket 34x96 Ovolo Flat Panel | 0' - 8 11/16" | Nantucket - Five Lite | 8' - 0" | No | No | 77105 | 4 | 0 | 8' - 2" | 3' - 2" | 0' - 4 15/16" | No | 2' - 10" |
| 77105 Nantucket 36x80 Ovolo Flat Panel | 0' - 8 11/16" | Nantucket - Five Lite | 6' - 8" | No | No | 77105 | 4 | 0 | 6' - 10" | 3' - 4" | 0' - 4 15/16" | No | 3' - 0" |
| 77105 Nantucket 36x84 Ovolo Flat Panel | 0' - 8 11/16" | Nantucket - Five Lite | 7' - 0" | No | No | 77105 | 4 | 0 | 7' - 2" | 3' - 4" | 0' - 4 15/16" | No | 3' - 0" |
| 77105 Nantucket 36x96 Ovolo Flat Panel | 0' - 8 11/16" | Nantucket - Five Lite | 8' - 0" | No | No | 77105 | 4 | 0 | 8' - 2" | 3' - 4" | 0' - 4 15/16" | No | 3' - 0" |
| 77105 Nantucket 38x80 Ovolo Flat Panel | 0' - 8 11/16" | Nantucket - Five Lite | 6' - 8" | No | No | 77105 | 4 | 0 | 6' - 10" | 3' - 6" | 0' - 4 15/16" | No | 3' - 2" |
| 77105 Nantucket 38x84 Ovolo Flat Panel | 0' - 8 11/16" | Nantucket - Five Lite | 7' - 0" | No | No | 77105 | 4 | 0 | 7' - 2" | 3' - 6" | 0' - 4 15/16" | No | 3' - 2" |
| 77105 Nantucket 38x96 Ovolo Flat Panel | 0' - 8 11/16" | Nantucket - Five Lite | 8' - 0" | No | No | 77105 | 4 | 0 | 8' - 2" | 3' - 6" | 0' - 4 15/16" | No | 3' - 2" |
| 77105 Nantucket 40x80 Ovolo Flat Panel | 0' - 8 11/16" | Nantucket - Five Lite | 6' - 8" | No | No | 77105 | 4 | 0 | 6' - 10" | 3' - 8" | 0' - 4 15/16" | No | 3' - 4" |
| 77105 Nantucket 40x84 Ovolo Flat Panel | 0' - 8 11/16" | Nantucket - Five Lite | 7' - 0" | No | No | 77105 | 4 | 0 | 7' - 2" | 3' - 8" | 0' - 4 15/16" | No | 3' - 4" |
| 77105 Nantucket 40x96 Ovolo Flat Panel | 0' - 8 11/16" | Nantucket - Five Lite | 8' - 0" | No | No | 77105 | 4 | 0 | 8' - 2" | 3' - 8" | 0' - 4 15/16" | No | 3' - 4" |
| 77106 Nantucket 30x80 Ovolo Flat Panel | 0' - 8 11/16" | Nantucket - Six Lite | 6' - 8" | No | No | 77106 | 2 | 1 | 6' - 10" | 2' - 10" | 0' - 4 15/16" | No | 2' - 6" |
| 77106 Nantucket 30x84 Ovolo Flat Panel | 0' - 8 11/16" | Nantucket - Six Lite | 7' - 0" | No | No | 77106 | 2 | 1 | 7' - 2" | 2' - 10" | 0' - 4 15/16" | No | 2' - 6" |
| 77106 Nantucket 30x96 Ovolo Flat Panel | 0' - 8 11/16" | Nantucket - Six Lite | 8' - 0" | No | No | 77106 | 2 | 1 | 8' - 2" | 2' - 10" | 0' - 4 15/16" | No | 2' - 6" |
| 77106 Nantucket 32x80 Ovolo Flat Panel | 0' - 8 11/16" | Nantucket - Six Lite | 6' - 8" | No | No | 77106 | 2 | 1 | 6' - 10" | 3' - 0" | 0' - 4 15/16" | No | 2' - 8" |
| 77106 Nantucket 32x84 Ovolo Flat Panel | 0' - 8 11/16" | Nantucket - Six Lite | 7' - 0" | No | No | 77106 | 2 | 1 | 7' - 2" | 3' - 0" | 0' - 4 15/16" | No | 2' - 8" |
| 77106 Nantucket 32x96 Ovolo Flat Panel | 0' - 8 11/16" | Nantucket - Six Lite | 8' - 0" | No | No | 77106 | 2 | 1 | 8' - 2" | 3' - 0" | 0' - 4 15/16" | No | 2' - 8" |
| 77106 Nantucket 34x80 Ovolo Flat Panel | 0' - 8 11/16" | Nantucket - Six Lite | 6' - 8" | No | No | 77106 | 2 | 1 | 6' - 10" | 3' - 2" | 0' - 4 15/16" | No | 2' - 10" |
| 77106 Nantucket 34x84 Ovolo Flat Panel | 0' - 8 11/16" | Nantucket - Six Lite | 7' - 0" | No | No | 77106 | 2 | 1 | 7' - 2" | 3' - 2" | 0' - 4 15/16" | No | 2' - 10" |
| 77106 Nantucket 34x96 Ovolo Flat Panel | 0' - 8 11/16" | Nantucket - Six Lite | 8' - 0" | No | No | 77106 | 2 | 1 | 8' - 2" | 3' - 2" | 0' - 4 15/16" | No | 2' - 10" |
| 77106 Nantucket 36x80 Ovolo Flat Panel | 0' - 8 11/16" | Nantucket - Six Lite | 6' - 8" | No | No | 77106 | 2 | 1 | 6' - 10" | 3' - 4" | 0' - 4 15/16" | No | 3' - 0" |
| 77106 Nantucket 36x84 Ovolo Flat Panel | 0' - 8 11/16" | Nantucket - Six Lite | 7' - 0" | No | No | 77106 | 2 | 1 | 7' - 2" | 3' - 4" | 0' - 4 15/16" | No | 3' - 0" |
| 77106 Nantucket 36x96 Ovolo Flat Panel | 0' - 8 11/16" | Nantucket - Six Lite | 8' - 0" | No | No | 77106 | 2 | 1 | 8' - 2" | 3' - 4" | 0' - 4 15/16" | No | 3' - 0" |
| 77106 Nantucket 38x80 Ovolo Flat Panel | 0' - 8 11/16" | Nantucket - Six Lite | 6' - 8" | No | No | 77106 | 2 | 1 | 6' - 10" | 3' - 6" | 0' - 4 15/16" | No | 3' - 2" |
| 77106 Nantucket 38x84 Ovolo Flat Panel | 0' - 8 11/16" | Nantucket - Six Lite | 7' - 0" | No | No | 77106 | 2 | 1 | 7' - 2" | 3' - 6" | 0' - 4 15/16" | No | 3' - 2" |
| 77106 Nantucket 38x96 Ovolo Flat Panel | 0' - 8 11/16" | Nantucket - Six Lite | 8' - 0" | No | No | 77106 | 2 | 1 | 8' - 2" | 3' - 6" | 0' - 4 15/16" | No | 3' - 2" |
| 77106 Nantucket 40x80 Ovolo Flat Panel | 0' - 8 11/16" | Nantucket - Six Lite | 6' - 8" | No | No | 77106 | 2 | 1 | 6' - 10" | 3' - 8" | 0' - 4 15/16" | No | 3' - 4" |
| 77106 Nantucket 40x84 Ovolo Flat Panel | 0' - 8 11/16" | Nantucket - Six Lite | 7' - 0" | No | No | 77106 | 2 | 1 | 7' - 2" | 3' - 8" | 0' - 4 15/16" | No | 3' - 4" |
| 77106 Nantucket 40x96 Ovolo Flat Panel | 0' - 8 11/16" | Nantucket - Six Lite | 8' - 0" | No | No | 77106 | 2 | 1 | 8' - 2" | 3' - 8" | 0' - 4 15/16" | No | 3' - 4" |
| 77108 Nantucket 30x80 Ovolo Flat Panel | 0' - 8 11/16" | Nantucket - Eight Lite | 6' - 8" | No | No | 77108 | 3 | 1 | 6' - 10" | 2' - 10" | 0' - 4 15/16" | No | 2' - 6" |
| 77108 Nantucket 30x84 Ovolo Flat Panel | 0' - 8 11/16" | Nantucket - Eight Lite | 7' - 0" | No | No | 77108 | 3 | 1 | 7' - 2" | 2' - 10" | 0' - 4 15/16" | No | 2' - 6" |
| 77108 Nantucket 30x96 Ovolo Flat Panel | 0' - 8 11/16" | Nantucket - Eight Lite | 8' - 0" | No | No | 77108 | 3 | 1 | 8' - 2" | 2' - 10" | 0' - 4 15/16" | No | 2' - 6" |
| 77108 Nantucket 32x80 Ovolo Flat Panel | 0' - 8 11/16" | Nantucket - Eight Lite | 6' - 8" | No | No | 77108 | 3 | 1 | 6' - 10" | 3' - 0" | 0' - 4 15/16" | No | 2' - 8" |
| 77108 Nantucket 32x84 Ovolo Flat Panel | 0' - 8 11/16" | Nantucket - Eight Lite | 7' - 0" | No | No | 77108 | 3 | 1 | 7' - 2" | 3' - 0" | 0' - 4 15/16" | No | 2' - 8" |
| 77108 Nantucket 32x96 Ovolo Flat Panel | 0' - 8 11/16" | Nantucket - Eight Lite | 8' - 0" | No | No | 77108 | 3 | 1 | 8' - 2" | 3' - 0" | 0' - 4 15/16" | No | 2' - 8" |
| 77108 Nantucket 34x80 Ovolo Flat Panel | 0' - 8 11/16" | Nantucket - Eight Lite | 6' - 8" | No | No | 77108 | 3 | 1 | 6' - 10" | 3' - 2" | 0' - 4 15/16" | No | 2' - 10" |
| 77108 Nantucket 34x84 Ovolo Flat Panel | 0' - 8 11/16" | Nantucket - Eight Lite | 7' - 0" | No | No | 77108 | 3 | 1 | 7' - 2" | 3' - 2" | 0' - 4 15/16" | No | 2' - 10" |
| 77108 Nantucket 34x96 Ovolo Flat Panel | 0' - 8 11/16" | Nantucket - Eight Lite | 8' - 0" | No | No | 77108 | 3 | 1 | 8' - 2" | 3' - 2" | 0' - 4 15/16" | No | 2' - 10" |
| 77108 Nantucket 36x80 Ovolo Flat Panel | 0' - 8 11/16" | Nantucket - Eight Lite | 6' - 8" | No | No | 77108 | 3 | 1 | 6' - 10" | 3' - 4" | 0' - 4 15/16" | No | 3' - 0" |
| 77108 Nantucket 36x84 Ovolo Flat Panel | 0' - 8 11/16" | Nantucket - Eight Lite | 7' - 0" | No | No | 77108 | 3 | 1 | 7' - 2" | 3' - 4" | 0' - 4 15/16" | No | 3' - 0" |
| 77108 Nantucket 36x96 Ovolo Flat Panel | 0' - 8 11/16" | Nantucket - Eight Lite | 8' - 0" | No | No | 77108 | 3 | 1 | 8' - 2" | 3' - 4" | 0' - 4 15/16" | No | 3' - 0" |
| 77108 Nantucket 38x80 Ovolo Flat Panel | 0' - 8 11/16" | Nantucket - Eight Lite | 6' - 8" | No | No | 77108 | 3 | 1 | 6' - 10" | 3' - 6" | 0' - 4 15/16" | No | 3' - 2" |
| 77108 Nantucket 38x84 Ovolo Flat Panel | 0' - 8 11/16" | Nantucket - Eight Lite | 7' - 0" | No | No | 77108 | 3 | 1 | 7' - 2" | 3' - 6" | 0' - 4 15/16" | No | 3' - 2" |
| 77108 Nantucket 38x96 Ovolo Flat Panel | 0' - 8 11/16" | Nantucket - Eight Lite | 8' - 0" | No | No | 77108 | 3 | 1 | 8' - 2" | 3' - 6" | 0' - 4 15/16" | No | 3' - 2" |
| 77108 Nantucket 40x80 Ovolo Flat Panel | 0' - 8 11/16" | Nantucket - Eight Lite | 6' - 8" | No | No | 77108 | 3 | 1 | 6' - 10" | 3' - 8" | 0' - 4 15/16" | No | 3' - 4" |
| 77108 Nantucket 40x84 Ovolo Flat Panel | 0' - 8 11/16" | Nantucket - Eight Lite | 7' - 0" | No | No | 77108 | 3 | 1 | 7' - 2" | 3' - 8" | 0' - 4 15/16" | No | 3' - 4" |
| 77108 Nantucket 40x96 Ovolo Flat Panel | 0' - 8 11/16" | Nantucket - Eight Lite | 8' - 0" | No | No | 77108 | 3 | 1 | 8' - 2" | 3' - 8" | 0' - 4 15/16" | No | 3' - 4" |
| 77109 Nantucket 30x80 Ovolo Flat Panel | 0' - 8 11/16" | Nantucket - Nine Lite | 6' - 8" | Yes | No | 77109 | 0 | 0 | 6' - 10" | 2' - 10" | 0' - 4 15/16" | Yes | 2' - 6" |
| 77109 Nantucket 30x84 Ovolo Flat Panel | 0' - 8 11/16" | Nantucket - Nine Lite | 7' - 0" | Yes | No | 77109 | 0 | 0 | 7' - 2" | 2' - 10" | 0' - 4 15/16" | Yes | 2' - 6" |
| 77109 Nantucket 30x96 Ovolo Flat Panel | 0' - 8 11/16" | Nantucket - Nine Lite | 8' - 0" | Yes | No | 77109 | 0 | 0 | 8' - 2" | 2' - 10" | 0' - 4 15/16" | Yes | 2' - 6" |
| 77109 Nantucket 32x80 Ovolo Flat Panel | 0' - 8 11/16" | Nantucket - Nine Lite | 6' - 8" | Yes | No | 77109 | 0 | 0 | 6' - 10" | 3' - 0" | 0' - 4 15/16" | Yes | 2' - 8" |
| 77109 Nantucket 32x84 Ovolo Flat Panel | 0' - 8 11/16" | Nantucket - Nine Lite | 7' - 0" | Yes | No | 77109 | 0 | 0 | 7' - 2" | 3' - 0" | 0' - 4 15/16" | Yes | 2' - 8" |
| 77109 Nantucket 32x96 Ovolo Flat Panel | 0' - 8 11/16" | Nantucket - Nine Lite | 8' - 0" | Yes | No | 77109 | 0 | 0 | 8' - 2" | 3' - 0" | 0' - 4 15/16" | Yes | 2' - 8" |
| 77109 Nantucket 34x80 Ovolo Flat Panel | 0' - 8 11/16" | Nantucket - Nine Lite | 6' - 8" | Yes | No | 77109 | 0 | 0 | 6' - 10" | 3' - 2" | 0' - 4 15/16" | Yes | 2' - 10" |
| 77109 Nantucket 34x84 Ovolo Flat Panel | 0' - 8 11/16" | Nantucket - Nine Lite | 7' - 0" | Yes | No | 77109 | 0 | 0 | 7' - 2" | 3' - 2" | 0' - 4 15/16" | Yes | 2' - 10" |
| 77109 Nantucket 34x96 Ovolo Flat Panel | 0' - 8 11/16" | Nantucket - Nine Lite | 8' - 0" | Yes | No | 77109 | 0 | 0 | 8' - 2" | 3' - 2" | 0' - 4 15/16" | Yes | 2' - 10" |
| 77109 Nantucket 36x80 Ovolo Flat Panel | 0' - 8 11/16" | Nantucket - Eight Lite | 6' - 8" | Yes | No | 77109 | 0 | 0 | 6' - 10" | 3' - 4" | 0' - 4 15/16" | Yes | 3' - 0" |
| 77109 Nantucket 36x84 Ovolo Flat Panel | 0' - 8 11/16" | Nantucket - Nine Lite | 7' - 0" | Yes | No | 77109 | 0 | 0 | 7' - 2" | 3' - 4" | 0' - 4 15/16" | Yes | 3' - 0" |
| 77109 Nantucket 36x96 Ovolo Flat Panel | 0' - 8 11/16" | Nantucket - Nine Lite | 8' - 0" | Yes | No | 77109 | 0 | 0 | 8' - 2" | 3' - 4" | 0' - 4 15/16" | Yes | 3' - 0" |
| 77109 Nantucket 38x80 Ovolo Flat Panel | 0' - 8 11/16" | Nantucket - Nine Lite | 6' - 8" | Yes | No | 77109 | 0 | 0 | 6' - 10" | 3' - 6" | 0' - 4 15/16" | Yes | 3' - 2" |
| 77109 Nantucket 38x84 Ovolo Flat Panel | 0' - 8 11/16" | Nantucket - Nine Lite | 7' - 0" | Yes | No | 77109 | 0 | 0 | 7' - 2" | 3' - 6" | 0' - 4 15/16" | Yes | 3' - 2" |
| 77109 Nantucket 38x96 Ovolo Flat Panel | 0' - 8 11/16" | Nantucket - Nine Lite | 8' - 0" | Yes | No | 77109 | 0 | 0 | 8' - 2" | 3' - 6" | 0' - 4 15/16" | Yes | 3' - 2" |
| 77109 Nantucket 40x80 Ovolo Flat Panel | 0' - 8 11/16" | Nantucket - Nine Lite | 6' - 8" | Yes | No | 77109 | 0 | 0 | 6' - 10" | 3' - 8" | 0' - 4 15/16" | Yes | 3' - 4" |
| 77109 Nantucket 40x84 Ovolo Flat Panel | 0' - 8 11/16" | Nantucket - Nine Lite | 7' - 0" | Yes | No | 77109 | 0 | 0 | 7' - 2" | 3' - 8" | 0' - 4 15/16" | Yes | 3' - 4" |
| 77109 Nantucket 40x96 Ovolo Flat Panel | 0' - 8 11/16" | Nantucket - Nine Lite | 8' - 0" | Yes | No | 77109 | 0 | 0 | 8' - 2" | 3' - 8" | 0' - 4 15/16" | Yes | 3' - 4" |
| 77122 Nantucket 30x80 Ovolo Flat Panel | 0' - 8 11/16" | Nantucket - Four Lite | 6' - 8" | No | No | 77122 | 1 | 1 | 6' - 10" | 2' - 10" | 0' - 4 15/16" | No | 2' - 6" |
| 77122 Nantucket 30x84 Ovolo Flat Panel | 0' - 8 11/16" | Nantucket - Four Lite | 7' - 0" | No | No | 77122 | 1 | 1 | 7' - 2" | 2' - 10" | 0' - 4 15/16" | No | 2' - 6" |
| 77122 Nantucket 30x96 Ovolo Flat Panel | 0' - 8 11/16" | Nantucket - Four Lite | 8' - 0" | No | No | 77122 | 1 | 1 | 8' - 2" | 2' - 10" | 0' - 4 15/16" | No | 2' - 6" |
| 77122 Nantucket 32x80 Ovolo Flat Panel | 0' - 8 11/16" | Nantucket - Four Lite | 6' - 8" | No | No | 77122 | 1 | 1 | 6' - 10" | 3' - 0" | 0' - 4 15/16" | No | 2' - 8" |
| 77122 Nantucket 32x84 Ovolo Flat Panel | 0' - 8 11/16" | Nantucket - Four Lite | 7' - 0" | No | No | 77122 | 1 | 1 | 7' - 2" | 3' - 0" | 0' - 4 15/16" | No | 2' - 8" |
| 77122 Nantucket 32x96 Ovolo Flat Panel | 0' - 8 11/16" | Nantucket - Four Lite | 8' - 0" | No | No | 77122 | 1 | 1 | 8' - 2" | 3' - 0" | 0' - 4 15/16" | No | 2' - 8" |
| 77122 Nantucket 34x80 Ovolo Flat Panel | 0' - 8 11/16" | Nantucket - Four Lite | 6' - 8" | No | No | 77122 | 1 | 1 | 6' - 10" | 3' - 2" | 0' - 4 15/16" | No | 2' - 10" |
| 77122 Nantucket 34x84 Ovolo Flat Panel | 0' - 8 11/16" | Nantucket - Four Lite | 7' - 0" | No | No | 77122 | 1 | 1 | 7' - 2" | 3' - 2" | 0' - 4 15/16" | No | 2' - 10" |
| 77122 Nantucket 34x96 Ovolo Flat Panel | 0' - 8 11/16" | Nantucket - Four Lite | 8' - 0" | No | No | 77122 | 1 | 1 | 8' - 2" | 3' - 2" | 0' - 4 15/16" | No | 2' - 10" |
| 77122 Nantucket 36x80 Ovolo Flat Panel | 0' - 8 11/16" | Nantucket - Four Lite | 6' - 8" | No | No | 77122 | 1 | 1 | 6' - 10" | 3' - 4" | 0' - 4 15/16" | No | 3' - 0" |
| 77122 Nantucket 36x84 Ovolo Flat Panel | 0' - 8 11/16" | Nantucket - Four Lite | 7' - 0" | No | No | 77122 | 1 | 1 | 7' - 2" | 3' - 4" | 0' - 4 15/16" | No | 3' - 0" |
| 77122 Nantucket 36x96 Ovolo Flat Panel | 0' - 8 11/16" | Nantucket - Four Lite | 8' - 0" | No | No | 77122 | 1 | 1 | 8' - 2" | 3' - 4" | 0' - 4 15/16" | No | 3' - 0" |
| 77122 Nantucket 38x80 Ovolo Flat Panel | 0' - 8 11/16" | Nantucket - Four Lite | 6' - 8" | No | No | 77122 | 1 | 1 | 6' - 10" | 3' - 6" | 0' - 4 15/16" | No | 3' - 2" |
| 77122 Nantucket 38x84 Ovolo Flat Panel | 0' - 8 11/16" | Nantucket - Four Lite | 7' - 0" | No | No | 77122 | 1 | 1 | 7' - 2" | 3' - 6" | 0' - 4 15/16" | No | 3' - 2" |
| 77122 Nantucket 38x96 Ovolo Flat Panel | 0' - 8 11/16" | Nantucket - Four Lite | 8' - 0" | No | No | 77122 | 1 | 1 | 8' - 2" | 3' - 6" | 0' - 4 15/16" | No | 3' - 2" |
| 77122 Nantucket 40x80 Ovolo Flat Panel | 0' - 8 11/16" | Nantucket - Four Lite | 6' - 8" | No | No | 77122 | 1 | 1 | 6' - 10" | 3' - 8" | 0' - 4 15/16" | No | 3' - 4" |
| 77122 Nantucket 40x84 Ovolo Flat Panel | 0' - 8 11/16" | Nantucket - Four Lite | 7' - 0" | No | No | 77122 | 1 | 1 | 7' - 2" | 3' - 8" | 0' - 4 15/16" | No | 3' - 4" |
| 77122 Nantucket 40x96 Ovolo Flat Panel | 0' - 8 11/16" | Nantucket - Four Lite | 8' - 0" | No | No | 77122 | 1 | 1 | 8' - 2" | 3' - 8" | 0' - 4 15/16" | No | 3' - 4" |

## geometry (parser evidence)
native form markers: Blend x8, Sweep x18
no freeform markers — native parametric forms only
